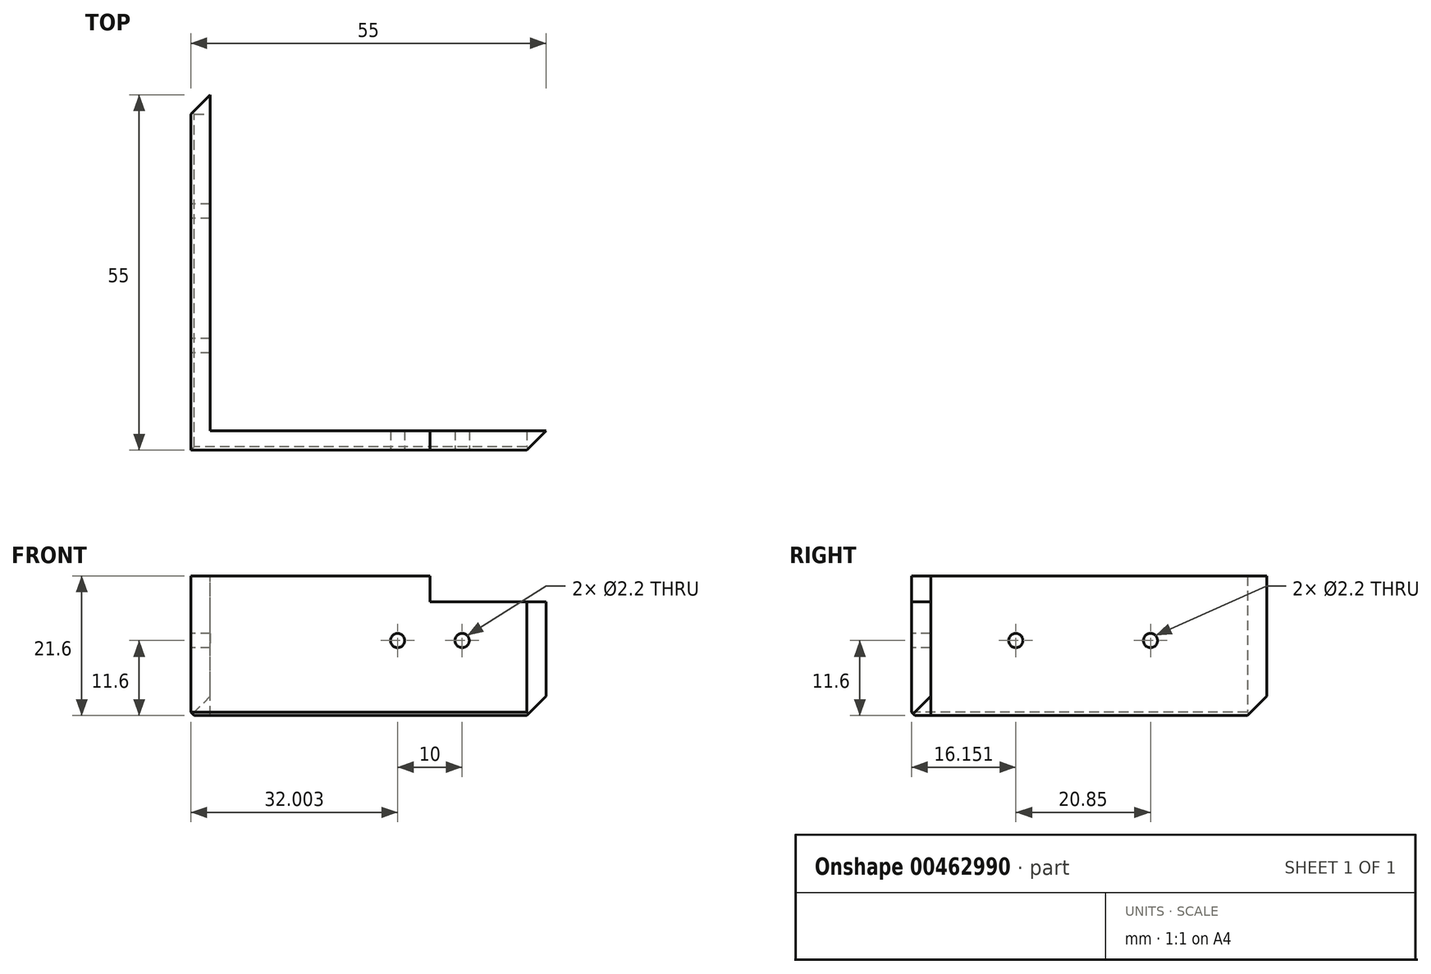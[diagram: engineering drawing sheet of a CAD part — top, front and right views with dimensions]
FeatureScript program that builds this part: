
annotation { "Feature Type Name" : "Feature", "Feature Type Description" : "" }
export const myFeature = defineFeature(function(context is Context, id is Id, definition is map)
    precondition{}
    {
        {
            var Q0;
            Q0=qCreatedBy(makeId("Top.planeOp"),FACE);
            var sketch = newSketch(context, id + "F0", { "sketchPlane" : qUnion([Q0])});
            skLineSegment(sketch, "E0.bottom", {"start": v(-12.1, -14.64) * mm, "end": v(42.9, -14.64) * mm});
            skLineSegment(sketch, "E0.left", {"start": v(-12.1, -14.64) * mm, "end": v(-12.1, 40.36) * mm});
            skLineSegment(sketch, "E1", {"start": v(-12.1, 40.36) * mm, "end": v(10.4, 40.36) * mm});
            skLineSegment(sketch, "E2", {"start": v(10.4, 40.36) * mm, "end": v(42.9, 7.86) * mm});
            skLineSegment(sketch, "E3", {"start": v(42.9, 7.86) * mm, "end": v(42.9, -14.64) * mm});
            skSolve(sketch);
        }
        {
            var Q0;
            Q0 = qSketchRegion(id + "F0", true);
            extrude(context, id + "F1", {"entities" : qUnion([Q0]), "depth" : 21.6 * mm, "offsetDistance" : 25 * mm});
        }
        {
            var Q0;
            Q0=makeQuery(id+"F1.opExtrude","CAP_FACE",FACE,{"disambiguationData":[OSD([sQuery(id+"F0.wireOp",EDGE,"E0.bottom"),sQuery(id+"F0.wireOp",EDGE,"E0.left"),sQuery(id+"F0.wireOp",EDGE,"E1"),sQuery(id+"F0.wireOp",EDGE,"E2"),sQuery(id+"F0.wireOp",EDGE,"E3")])],"isStart":false});
            var sketch = newSketch(context, id + "F2", { "sketchPlane" : qUnion([Q0])});
            skLineSegment(sketch, "E4.bottom", {"start": v(-9.1, 40.36) * mm, "end": v(42.9, 40.36) * mm});
            skLineSegment(sketch, "E4.top", {"start": v(-9.1, -11.64) * mm, "end": v(42.9, -11.64) * mm});
            skLineSegment(sketch, "E4.left", {"start": v(-9.1, 40.36) * mm, "end": v(-9.1, -11.64) * mm});
            skLineSegment(sketch, "E4.right", {"start": v(42.9, 40.36) * mm, "end": v(42.9, -11.64) * mm});
            skSolve(sketch);
        }
        {
            var Q0;
            Q0 = qSketchRegion(id + "F2", true);
            extrude(context, id + "F3", {"entities" : qUnion([Q0]), "operationType" : NewBodyOperationType.REMOVE, "oppositeDirection" : true, "depth" : 22 * mm, "offsetDistance" : 25 * mm});
        }
        {
            var Q0;
            Q0=makeQuery(id+"F1.opExtrude","CAP_EDGE",EDGE,{"disambiguationData":[OSD([sQuery(id+"F0.wireOp",EDGE,"E3")])],"isStart":true});
            var Q1;
            Q1=makeQuery(id+"F1.opExtrude","CAP_EDGE",EDGE,{"disambiguationData":[OSD([sQuery(id+"F0.wireOp",EDGE,"E2")])],"isStart":true});
            var Q2;
            Q2=makeQuery(id+"F1.opExtrude","CAP_EDGE",EDGE,{"disambiguationData":[OSD([sQuery(id+"F0.wireOp",EDGE,"E1")])],"isStart":true});
            var Q3;
            Q3=makeQuery(id+"F1.opExtrude","SWEPT_EDGE",EDGE,{"disambiguationData":[OSD([sQuery(id+"F0.wireOp",EDGE,"E0.left"),sQuery(id+"F0.wireOp",EDGE,"E1")])]});
            var Q4;
            Q4=makeQuery(id+"F1.opExtrude","SWEPT_EDGE",EDGE,{"disambiguationData":[OSD([sQuery(id+"F0.wireOp",EDGE,"E0.bottom"),sQuery(id+"F0.wireOp",EDGE,"E3")])]});
            chamfer(context, id + "F4", {"entities" : qUnion([Q0, Q1, Q2, Q3, Q4]), "width" : 3 * mm, "tangentPropagation" : true});
        }
        {
            var Q0;
            Q0=makeQuery(id+"F1.opExtrude","CAP_EDGE",EDGE,{"disambiguationData":[OSD([sQuery(id+"F0.wireOp",EDGE,"E0.bottom")])],"isStart":true});
            var Q1;
            Q1=makeQuery(id+"F1.opExtrude","CAP_EDGE",EDGE,{"disambiguationData":[OSD([sQuery(id+"F0.wireOp",EDGE,"E0.left")])],"isStart":true});
            chamfer(context, id + "F5", {"entities" : qUnion([Q0, Q1]), "width" : 0.5 * mm, "tangentPropagation" : true});
        }
        {
            var Q0;
            Q0=makeQuery(id+"F1.opExtrude","SWEPT_FACE",FACE,{"disambiguationData":[OSD([sQuery(id+"F0.wireOp",EDGE,"E0.bottom")])]});
            var sketch = newSketch(context, id + "F6", { "sketchPlane" : qUnion([Q0])});
            skCircle(sketch, "E5", {"center": v(29.9, 11.6) * mm, "radius": 1.1 * mm});
            skCircle(sketch, "E6", {"center": v(19.9, 11.6) * mm, "radius": 1.1 * mm});
            skSolve(sketch);
        }
        {
            var Q0;
            Q0 = qSketchRegion(id + "F6", true);
            extrude(context, id + "F7", {"entities" : qUnion([Q0]), "operationType" : NewBodyOperationType.REMOVE, "oppositeDirection" : true, "depth" : 3 * mm, "offsetDistance" : 25 * mm});
        }
        {
            var Q0;
            Q0=makeQuery(id+"F1.opExtrude","SWEPT_FACE",FACE,{"disambiguationData":[OSD([sQuery(id+"F0.wireOp",EDGE,"E0.left")])]});
            var sketch = newSketch(context, id + "F8", { "sketchPlane" : qUnion([Q0])});
            skCircle(sketch, "E7", {"center": v(-22.36, 11.6) * mm, "radius": 1.1 * mm});
            skCircle(sketch, "E8", {"center": v(-1.51, 11.6) * mm, "radius": 1.1 * mm});
            skSolve(sketch);
        }
        {
            var Q0;
            Q0 = qSketchRegion(id + "F8", true);
            extrude(context, id + "F9", {"entities" : qUnion([Q0]), "operationType" : NewBodyOperationType.REMOVE, "oppositeDirection" : true, "depth" : 3 * mm, "offsetDistance" : 25 * mm});
        }
        {
            var Q0;
            Q0=makeQuery(id+"F3.boolean.opBoolean","COPY",FACE,{"derivedFrom":makeQuery(id+"F3.opExtrude","SWEPT_FACE",FACE,{"disambiguationData":[OSD([sQuery(id+"F2.wireOp",EDGE,"E4.top")])]})});
            var sketch = newSketch(context, id + "F10", { "sketchPlane" : qUnion([Q0])});
            skLineSegment(sketch, "E9.bottom", {"start": v(-42.9, 21.6) * mm, "end": v(-24.9, 21.6) * mm});
            skLineSegment(sketch, "E9.top", {"start": v(-42.9, 17.6) * mm, "end": v(-24.9, 17.6) * mm});
            skLineSegment(sketch, "E9.left", {"start": v(-42.9, 21.6) * mm, "end": v(-42.9, 17.6) * mm});
            skLineSegment(sketch, "E9.right", {"start": v(-24.9, 21.6) * mm, "end": v(-24.9, 17.6) * mm});
            skSolve(sketch);
        }
        {
            var Q0;
            Q0 = qSketchRegion(id + "F10", true);
            extrude(context, id + "F11", {"entities" : qUnion([Q0]), "operationType" : NewBodyOperationType.REMOVE, "oppositeDirection" : true, "depth" : 3 * mm, "offsetDistance" : 25 * mm});
        }
    });
